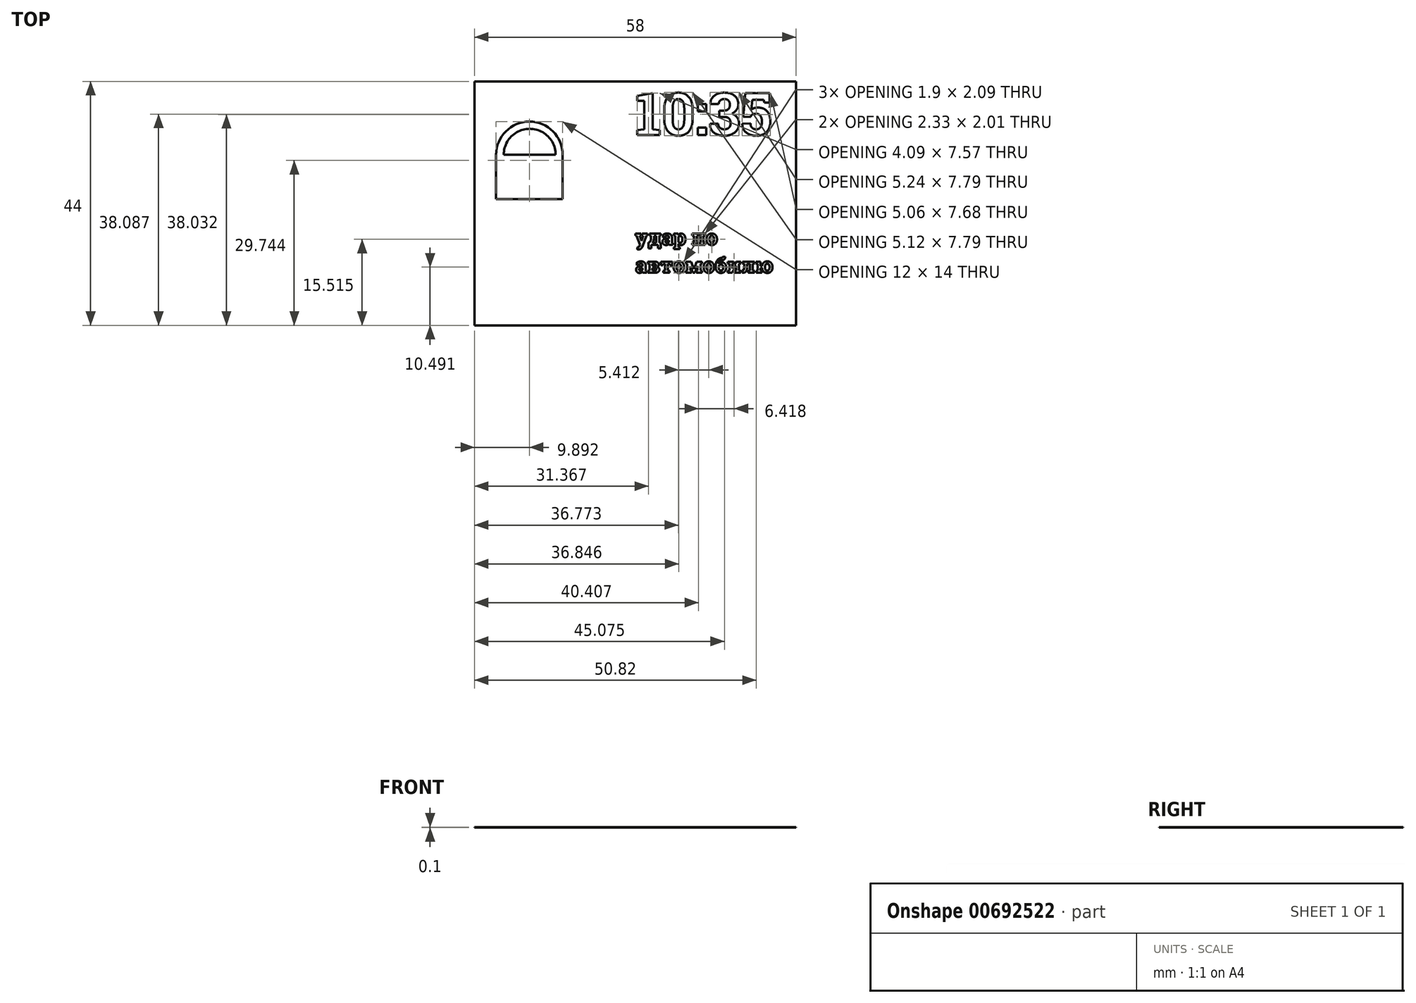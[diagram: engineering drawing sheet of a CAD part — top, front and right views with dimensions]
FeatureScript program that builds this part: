
annotation { "Feature Type Name" : "Feature", "Feature Type Description" : "" }
export const myFeature = defineFeature(function(context is Context, id is Id, definition is map)
    precondition{}
    {
        {
            var Q0;
            Q0=qCreatedBy(makeId("Top.planeOp"),FACE);
            var sketch = newSketch(context, id + "F0", { "sketchPlane" : qUnion([Q0])});
            skPoint(sketch, "E0.middle", {"position": v(0, 0) * mm});
            skLineSegment(sketch, "E1.bottom", {"start": v(-23.73, 8.74) * mm, "end": v(-14.36, 8.74) * mm});
            skLineSegment(sketch, "E1.top", {"start": v(-25.1, 0.74) * mm, "end": v(-13.1, 0.74) * mm});
            skLineSegment(sketch, "E1.left", {"start": v(-25.1, 8.74) * mm, "end": v(-25.1, 0.74) * mm});
            skLineSegment(sketch, "E1.right", {"start": v(-13.1, 8.74) * mm, "end": v(-13.1, 0.74) * mm});
            skArc(sketch, "E2", {"start": v(-13.1, 8.74) * mm, "mid": v(-19.1, 14.74) * mm, "end": v(-25.1, 8.74) * mm});
            skArc(sketch, "E3", {"start": v(-14.36, 8.74) * mm, "mid": v(-19.05, 13.44) * mm, "end": v(-23.73, 8.74) * mm});
            skText(sketch, "E4", { "text": "10:35", "fontName": "RobotoSlab-Bold.ttf"});
            skText(sketch, "E5", { "text": "удар по \nавтомобилю", "fontName": "RobotoSlab-Bold.ttf"});
            const initialGuessF0  = {"E4": [0, 0.0123, 1, 0, 0.00767], "E5": [0, -0.00749, 1, 0, 0.00274]};
            skSetInitialGuess(sketch, initialGuessF0);
            skSolve(sketch);
        }
        {
            var Q0;
            Q0=qCreatedBy(makeId("Top.planeOp"),FACE);
            var sketch = newSketch(context, id + "F1", { "sketchPlane" : qUnion([Q0])});
            skLineSegment(sketch, "E6.bottom", {"start": v(29, 22) * mm, "end": v(-29, 22) * mm});
            skLineSegment(sketch, "E6.top", {"start": v(29, -22) * mm, "end": v(-29, -22) * mm});
            skLineSegment(sketch, "E6.left", {"start": v(29, 22) * mm, "end": v(29, -22) * mm});
            skLineSegment(sketch, "E6.right", {"start": v(-29, 22) * mm, "end": v(-29, -22) * mm});
            skPoint(sketch, "E6.middle", {"position": v(0, 0) * mm});
            skSolve(sketch);
        }
        {
            var Q0;
            Q0 = qSketchRegion(id + "F1", true);
            extrude(context, id + "F2", {"entities" : qUnion([Q0]), "depth" : 0.1 * mm, "offsetDistance" : 25 * mm});
        }
        {
            var Q0;
            Q0 = qSketchRegion(id + "F0", true);
            var Q1;
            Q1=makeQuery(id+"F2.opExtrude","SWEPT_BODY",BODY,{"disambiguationData":[OSD([sQuery(id+"F1.wireOp",EDGE,"E6.bottom"),sQuery(id+"F1.wireOp",EDGE,"E6.top"),sQuery(id+"F1.wireOp",EDGE,"E6.left"),sQuery(id+"F1.wireOp",EDGE,"E6.right")])]});
            extrude(context, id + "F3", {"entities" : qUnion([Q0]), "operationType" : NewBodyOperationType.REMOVE, "endBound" : BoundingType.UP_TO_BODY, "depth" : 1 * mm, "endBoundEntityBody" : qUnion([Q1]), "offsetDistance" : 25 * mm});
        }
    });
